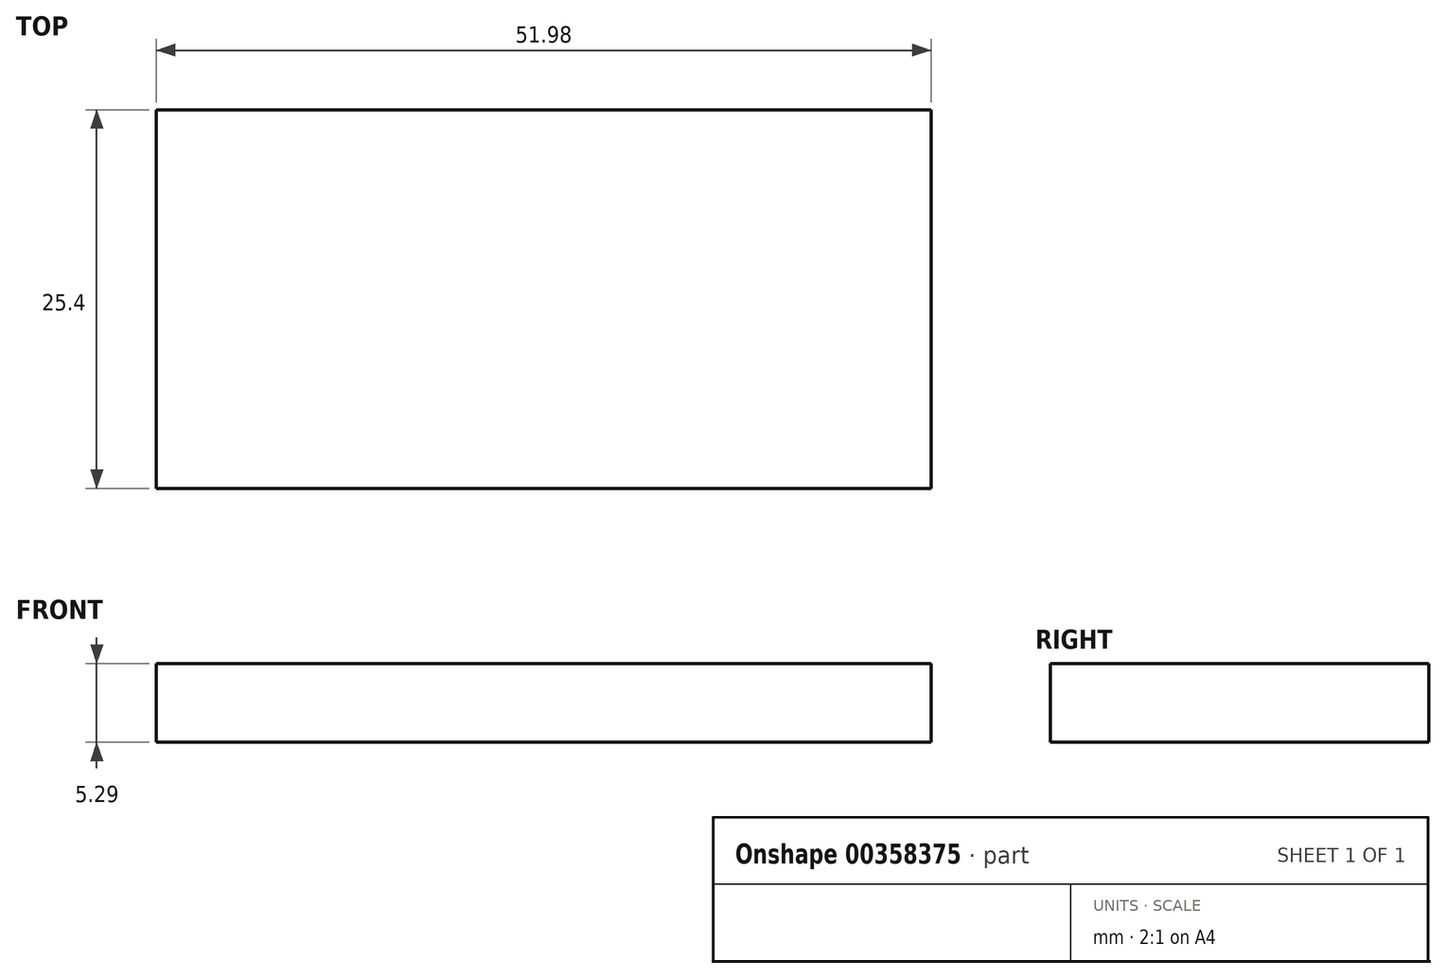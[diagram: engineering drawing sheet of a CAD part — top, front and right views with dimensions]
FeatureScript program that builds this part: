
annotation { "Feature Type Name" : "Feature", "Feature Type Description" : "" }
export const myFeature = defineFeature(function(context is Context, id is Id, definition is map)
    precondition{}
    {
        {
            var Q0;
            Q0=qCreatedBy(makeId("Front.planeOp"),FACE);
            var sketch = newSketch(context, id + "F0", { "sketchPlane" : qUnion([Q0])});
            skLineSegment(sketch, "E0.bottom", {"start": v(65, 37.34) * mm, "end": v(13, 37.34) * mm});
            skLineSegment(sketch, "E0.top", {"start": v(65, 42.63) * mm, "end": v(13, 42.63) * mm});
            skLineSegment(sketch, "E0.left", {"start": v(65, 37.34) * mm, "end": v(65, 42.63) * mm});
            skLineSegment(sketch, "E0.right", {"start": v(13, 37.34) * mm, "end": v(13, 42.63) * mm});
            skPoint(sketch, "E0.middle", {"position": v(39, 39.99) * mm});
            skFitSpline(sketch, "E1", {"points": [v(-105.27, 1.61) * mm, v(13, 42.63) * mm], "startDerivative": vector(11.9, 130.41) * mm, "endDerivative": vector(-7.84, 116.18) * mm});
            skSolve(sketch);
        }
        {
            var Q0;
            Q0 = qSketchRegion(id + "F0", true);
            extrude(context, id + "F1", {"entities" : qUnion([Q0]), "depth" : 25.4 * mm});
        }
    });
